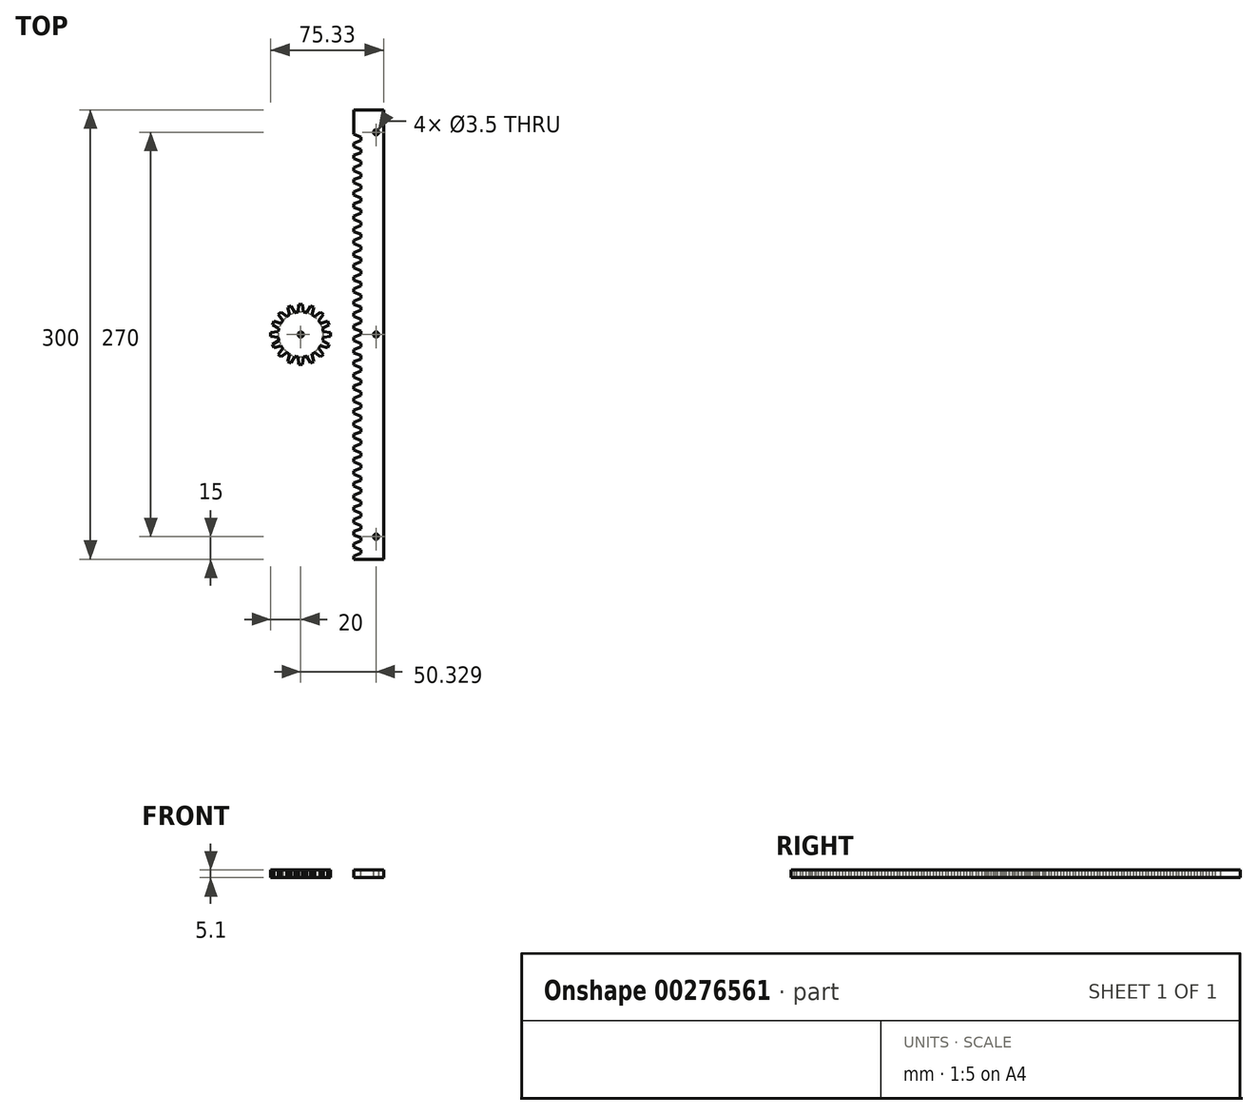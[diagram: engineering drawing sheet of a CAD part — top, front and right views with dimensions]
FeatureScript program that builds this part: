
annotation { "Feature Type Name" : "Feature", "Feature Type Description" : "" }
export const myFeature = defineFeature(function(context is Context, id is Id, definition is map)
    precondition{}
    {
        {
            var Q0;
            Q0=qCreatedBy(makeId("Top.planeOp"),FACE);
            var sketch = newSketch(context, id + "F0", { "sketchPlane" : qUnion([Q0])});
            skCircle(sketch, "E0", {"center": v(0, 0) * mm, "radius": 15 * mm});
            skSolve(sketch);
        }
        {
            var Q0;
            Q0=qSketchRegion(id+"F0",true);
            extrude(context, id + "F1", {"entities" : qUnion([Q0]), "depth" : .1 * mm});
        }
        {
            var Q0;
            Q0=makeQuery(id+"F1.opExtrude","CAP_FACE",FACE,{"disambiguationData":[OSD([sQuery(id+"F0.wireOp",EDGE,"E0")])],"isStart":false});
            var sketch = newSketch(context, id + "F2", { "sketchPlane" : qUnion([Q0])});
            skLineSegment(sketch, "E1", {"start": v(0, 0) * mm, "end": v(4.14, 32.55) * mm, "construction": true});
            skLineSegment(sketch, "E2", {"start": v(0, 0) * mm, "end": v(-4.14, 32.58) * mm, "construction": true});
            skLineSegment(sketch, "E3", {"start": v(-1.9, 14.88) * mm, "end": v(-1.24, 20) * mm});
            skLineSegment(sketch, "E4", {"start": v(-1.24, 20) * mm, "end": v(1.24, 20) * mm});
            skLineSegment(sketch, "E5", {"start": v(1.24, 20) * mm, "end": v(1.9, 14.88) * mm});
            skLineSegment(sketch, "E6.1.0", {"start": v(-7.44, 13.02) * mm, "end": v(-8.8, 18) * mm});
            skLineSegment(sketch, "E6.1.1", {"start": v(-6.5, 18.95) * mm, "end": v(-3.95, 14.47) * mm});
            skLineSegment(sketch, "E6.1.2", {"start": v(-8.8, 18) * mm, "end": v(-6.5, 18.95) * mm});
            skLineSegment(sketch, "E6.2.0", {"start": v(-11.86, 9.18) * mm, "end": v(-15.02, 13.26) * mm});
            skLineSegment(sketch, "E6.2.1", {"start": v(-13.26, 15.02) * mm, "end": v(-9.18, 11.86) * mm});
            skLineSegment(sketch, "E6.2.2", {"start": v(-15.02, 13.26) * mm, "end": v(-13.26, 15.02) * mm});
            skLineSegment(sketch, "E6.3.0", {"start": v(-14.47, 3.95) * mm, "end": v(-18.95, 6.5) * mm});
            skLineSegment(sketch, "E6.3.1", {"start": v(-18, 8.8) * mm, "end": v(-13.02, 7.44) * mm});
            skLineSegment(sketch, "E6.3.2", {"start": v(-18.95, 6.5) * mm, "end": v(-18, 8.8) * mm});
            skLineSegment(sketch, "E6.4.0", {"start": v(-14.88, -1.9) * mm, "end": v(-20, -1.24) * mm});
            skLineSegment(sketch, "E6.4.1", {"start": v(-20, 1.24) * mm, "end": v(-14.88, 1.9) * mm});
            skLineSegment(sketch, "E6.4.2", {"start": v(-20, -1.24) * mm, "end": v(-20, 1.24) * mm});
            skLineSegment(sketch, "E6.5.0", {"start": v(-13.02, -7.44) * mm, "end": v(-18, -8.8) * mm});
            skLineSegment(sketch, "E6.5.1", {"start": v(-18.95, -6.5) * mm, "end": v(-14.47, -3.95) * mm});
            skLineSegment(sketch, "E6.5.2", {"start": v(-18, -8.8) * mm, "end": v(-18.95, -6.5) * mm});
            skLineSegment(sketch, "E6.6.0", {"start": v(-9.18, -11.86) * mm, "end": v(-13.26, -15.02) * mm});
            skLineSegment(sketch, "E6.6.1", {"start": v(-15.02, -13.26) * mm, "end": v(-11.86, -9.18) * mm});
            skLineSegment(sketch, "E6.6.2", {"start": v(-13.26, -15.02) * mm, "end": v(-15.02, -13.26) * mm});
            skLineSegment(sketch, "E6.7.0", {"start": v(-3.95, -14.47) * mm, "end": v(-6.5, -18.95) * mm});
            skLineSegment(sketch, "E6.7.1", {"start": v(-8.8, -18) * mm, "end": v(-7.44, -13.02) * mm});
            skLineSegment(sketch, "E6.7.2", {"start": v(-6.5, -18.95) * mm, "end": v(-8.8, -18) * mm});
            skLineSegment(sketch, "E6.8.0", {"start": v(1.9, -14.88) * mm, "end": v(1.24, -20) * mm});
            skLineSegment(sketch, "E6.8.1", {"start": v(-1.24, -20) * mm, "end": v(-1.9, -14.88) * mm});
            skLineSegment(sketch, "E6.8.2", {"start": v(1.24, -20) * mm, "end": v(-1.24, -20) * mm});
            skLineSegment(sketch, "E6.9.0", {"start": v(7.44, -13.02) * mm, "end": v(8.8, -18) * mm});
            skLineSegment(sketch, "E6.9.1", {"start": v(6.5, -18.95) * mm, "end": v(3.95, -14.47) * mm});
            skLineSegment(sketch, "E6.9.2", {"start": v(8.8, -18) * mm, "end": v(6.5, -18.95) * mm});
            skLineSegment(sketch, "E6.10.0", {"start": v(11.86, -9.18) * mm, "end": v(15.02, -13.26) * mm});
            skLineSegment(sketch, "E6.10.1", {"start": v(13.26, -15.02) * mm, "end": v(9.18, -11.86) * mm});
            skLineSegment(sketch, "E6.10.2", {"start": v(15.02, -13.26) * mm, "end": v(13.26, -15.02) * mm});
            skLineSegment(sketch, "E6.11.0", {"start": v(14.47, -3.95) * mm, "end": v(18.95, -6.5) * mm});
            skLineSegment(sketch, "E6.11.1", {"start": v(18, -8.8) * mm, "end": v(13.02, -7.44) * mm});
            skLineSegment(sketch, "E6.11.2", {"start": v(18.95, -6.5) * mm, "end": v(18, -8.8) * mm});
            skLineSegment(sketch, "E6.12.0", {"start": v(14.88, 1.9) * mm, "end": v(20, 1.24) * mm});
            skLineSegment(sketch, "E6.12.1", {"start": v(20, -1.24) * mm, "end": v(14.88, -1.9) * mm});
            skLineSegment(sketch, "E6.12.2", {"start": v(20, 1.24) * mm, "end": v(20, -1.24) * mm});
            skLineSegment(sketch, "E6.13.0", {"start": v(13.02, 7.44) * mm, "end": v(18, 8.8) * mm});
            skLineSegment(sketch, "E6.13.1", {"start": v(18.95, 6.5) * mm, "end": v(14.47, 3.95) * mm});
            skLineSegment(sketch, "E6.13.2", {"start": v(18, 8.8) * mm, "end": v(18.95, 6.5) * mm});
            skLineSegment(sketch, "E6.14.0", {"start": v(9.18, 11.86) * mm, "end": v(13.26, 15.02) * mm});
            skLineSegment(sketch, "E6.14.1", {"start": v(15.02, 13.26) * mm, "end": v(11.86, 9.18) * mm});
            skLineSegment(sketch, "E6.14.2", {"start": v(13.26, 15.02) * mm, "end": v(15.02, 13.26) * mm});
            skLineSegment(sketch, "E6.15.0", {"start": v(3.95, 14.47) * mm, "end": v(6.5, 18.95) * mm});
            skLineSegment(sketch, "E6.15.1", {"start": v(8.8, 18) * mm, "end": v(7.44, 13.02) * mm});
            skLineSegment(sketch, "E6.15.2", {"start": v(6.5, 18.95) * mm, "end": v(8.8, 18) * mm});
            skPoint(sketch, "E6.center", {"position": v(0, 0) * mm});
            skCircle(sketch, "E7", {"center": v(0, 0) * mm, "radius": 15.15 * mm});
            skSolve(sketch);
        }
        {
            var Q0;
            Q0=qSketchRegion(id+"F2",true);
            extrude(context, id + "F3", {"entities" : qUnion([Q0]), "operationType" : NewBodyOperationType.ADD, "depth" : 5 * mm});
        }
        {
            var Q0;
            Q0=qCreatedBy(makeId("Top.planeOp"),FACE);
            var sketch = newSketch(context, id + "F4", { "sketchPlane" : qUnion([Q0])});
            skLineSegment(sketch, "E8.bottom", {"start": v(35.33, -150) * mm, "end": v(55.33, -150) * mm});
            skLineSegment(sketch, "E8.top", {"start": v(35.33, 150) * mm, "end": v(55.33, 150) * mm});
            skLineSegment(sketch, "E8.left", {"start": v(35.33, -150) * mm, "end": v(35.33, 150) * mm});
            skLineSegment(sketch, "E8.right", {"start": v(55.33, -150) * mm, "end": v(55.33, 150) * mm});
            skPoint(sketch, "E8.middle", {"position": v(45.33, 0) * mm});
            skSolve(sketch);
        }
        {
            var Q0;
            Q0=qSketchRegion(id+"F4",true);
            extrude(context, id + "F5", {"entities" : qUnion([Q0]), "depth" : 5 * mm});
        }
        {
            var Q0;
            Q0=makeQuery(id+"F5.opExtrude","CAP_FACE",FACE,{"disambiguationData":[OSD([sQuery(id+"F4.wireOp",EDGE,"E8.bottom"),sQuery(id+"F4.wireOp",EDGE,"E8.top"),sQuery(id+"F4.wireOp",EDGE,"E8.left"),sQuery(id+"F4.wireOp",EDGE,"E8.right")])],"isStart":false});
            var sketch = newSketch(context, id + "F6", { "sketchPlane" : qUnion([Q0])});
            skLineSegment(sketch, "E9", {"start": v(35.33, -147.77) * mm, "end": v(40.33, -145.95) * mm});
            skLineSegment(sketch, "E10", {"start": v(40.33, -145.95) * mm, "end": v(40.33, -143.72) * mm});
            skLineSegment(sketch, "E11", {"start": v(40.33, -143.72) * mm, "end": v(35.33, -141.9) * mm});
            skLineSegment(sketch, "E12", {"start": v(35.33, -147.77) * mm, "end": v(35.33, -150) * mm});
            skLineSegment(sketch, "E13.1.0.0", {"start": v(40.33, -135.62) * mm, "end": v(35.33, -133.8) * mm});
            skLineSegment(sketch, "E13.1.0.1", {"start": v(35.33, -139.67) * mm, "end": v(40.33, -137.85) * mm});
            skLineSegment(sketch, "E13.1.0.2", {"start": v(35.33, -139.67) * mm, "end": v(35.33, -141.9) * mm});
            skLineSegment(sketch, "E13.1.0.3", {"start": v(40.33, -137.85) * mm, "end": v(40.33, -135.62) * mm});
            skLineSegment(sketch, "E13.2.0.0", {"start": v(40.33, -127.51) * mm, "end": v(35.33, -125.7) * mm});
            skLineSegment(sketch, "E13.2.0.1", {"start": v(35.33, -131.56) * mm, "end": v(40.33, -129.75) * mm});
            skLineSegment(sketch, "E13.2.0.2", {"start": v(35.33, -131.56) * mm, "end": v(35.33, -133.8) * mm});
            skLineSegment(sketch, "E13.2.0.3", {"start": v(40.33, -129.75) * mm, "end": v(40.33, -127.51) * mm});
            skLineSegment(sketch, "E13.3.0.0", {"start": v(40.33, -119.41) * mm, "end": v(35.33, -117.6) * mm});
            skLineSegment(sketch, "E13.3.0.1", {"start": v(35.33, -123.46) * mm, "end": v(40.33, -121.64) * mm});
            skLineSegment(sketch, "E13.3.0.2", {"start": v(35.33, -123.46) * mm, "end": v(35.33, -125.7) * mm});
            skLineSegment(sketch, "E13.3.0.3", {"start": v(40.33, -121.64) * mm, "end": v(40.33, -119.41) * mm});
            skLineSegment(sketch, "E13.4.0.0", {"start": v(40.33, -111.31) * mm, "end": v(35.33, -109.5) * mm});
            skLineSegment(sketch, "E13.4.0.1", {"start": v(35.33, -115.36) * mm, "end": v(40.33, -113.54) * mm});
            skLineSegment(sketch, "E13.4.0.2", {"start": v(35.33, -115.36) * mm, "end": v(35.33, -117.6) * mm});
            skLineSegment(sketch, "E13.4.0.3", {"start": v(40.33, -113.54) * mm, "end": v(40.33, -111.31) * mm});
            skLineSegment(sketch, "E13.5.0.0", {"start": v(40.33, -103.2) * mm, "end": v(35.33, -101.39) * mm});
            skLineSegment(sketch, "E13.5.0.1", {"start": v(35.33, -107.26) * mm, "end": v(40.33, -105.44) * mm});
            skLineSegment(sketch, "E13.5.0.2", {"start": v(35.33, -107.26) * mm, "end": v(35.33, -109.5) * mm});
            skLineSegment(sketch, "E13.5.0.3", {"start": v(40.33, -105.44) * mm, "end": v(40.33, -103.2) * mm});
            skLineSegment(sketch, "E13.6.0.0", {"start": v(40.33, -95.1) * mm, "end": v(35.33, -93.29) * mm});
            skLineSegment(sketch, "E13.6.0.1", {"start": v(35.33, -99.16) * mm, "end": v(40.33, -97.34) * mm});
            skLineSegment(sketch, "E13.6.0.2", {"start": v(35.33, -99.16) * mm, "end": v(35.33, -101.39) * mm});
            skLineSegment(sketch, "E13.6.0.3", {"start": v(40.33, -97.34) * mm, "end": v(40.33, -95.1) * mm});
            skLineSegment(sketch, "E13.7.0.0", {"start": v(40.33, -87) * mm, "end": v(35.33, -85.18) * mm});
            skLineSegment(sketch, "E13.7.0.1", {"start": v(35.33, -91.05) * mm, "end": v(40.33, -89.24) * mm});
            skLineSegment(sketch, "E13.7.0.2", {"start": v(35.33, -91.05) * mm, "end": v(35.33, -93.29) * mm});
            skLineSegment(sketch, "E13.7.0.3", {"start": v(40.33, -89.24) * mm, "end": v(40.33, -87) * mm});
            skLineSegment(sketch, "E13.8.0.0", {"start": v(40.33, -78.9) * mm, "end": v(35.33, -77.08) * mm});
            skLineSegment(sketch, "E13.8.0.1", {"start": v(35.33, -82.95) * mm, "end": v(40.33, -81.13) * mm});
            skLineSegment(sketch, "E13.8.0.2", {"start": v(35.33, -82.95) * mm, "end": v(35.33, -85.18) * mm});
            skLineSegment(sketch, "E13.8.0.3", {"start": v(40.33, -81.13) * mm, "end": v(40.33, -78.9) * mm});
            skLineSegment(sketch, "E13.9.0.0", {"start": v(40.33, -70.8) * mm, "end": v(35.33, -68.98) * mm});
            skLineSegment(sketch, "E13.9.0.1", {"start": v(35.33, -74.85) * mm, "end": v(40.33, -73.03) * mm});
            skLineSegment(sketch, "E13.9.0.2", {"start": v(35.33, -74.85) * mm, "end": v(35.33, -77.08) * mm});
            skLineSegment(sketch, "E13.9.0.3", {"start": v(40.33, -73.03) * mm, "end": v(40.33, -70.8) * mm});
            skLineSegment(sketch, "E13.10.0.0", {"start": v(40.33, -62.7) * mm, "end": v(35.33, -60.88) * mm});
            skLineSegment(sketch, "E13.10.0.1", {"start": v(35.33, -66.75) * mm, "end": v(40.33, -64.93) * mm});
            skLineSegment(sketch, "E13.10.0.2", {"start": v(35.33, -66.75) * mm, "end": v(35.33, -68.98) * mm});
            skLineSegment(sketch, "E13.10.0.3", {"start": v(40.33, -64.93) * mm, "end": v(40.33, -62.7) * mm});
            skLineSegment(sketch, "E13.11.0.0", {"start": v(40.33, -54.6) * mm, "end": v(35.33, -52.78) * mm});
            skLineSegment(sketch, "E13.11.0.1", {"start": v(35.33, -58.65) * mm, "end": v(40.33, -56.83) * mm});
            skLineSegment(sketch, "E13.11.0.2", {"start": v(35.33, -58.65) * mm, "end": v(35.33, -60.88) * mm});
            skLineSegment(sketch, "E13.11.0.3", {"start": v(40.33, -56.83) * mm, "end": v(40.33, -54.6) * mm});
            skLineSegment(sketch, "E13.12.0.0", {"start": v(40.33, -46.5) * mm, "end": v(35.33, -44.67) * mm});
            skLineSegment(sketch, "E13.12.0.1", {"start": v(35.33, -50.54) * mm, "end": v(40.33, -48.73) * mm});
            skLineSegment(sketch, "E13.12.0.2", {"start": v(35.33, -50.54) * mm, "end": v(35.33, -52.78) * mm});
            skLineSegment(sketch, "E13.12.0.3", {"start": v(40.33, -48.73) * mm, "end": v(40.33, -46.5) * mm});
            skLineSegment(sketch, "E13.13.0.0", {"start": v(40.33, -38.4) * mm, "end": v(35.33, -36.57) * mm});
            skLineSegment(sketch, "E13.13.0.1", {"start": v(35.33, -42.44) * mm, "end": v(40.33, -40.62) * mm});
            skLineSegment(sketch, "E13.13.0.2", {"start": v(35.33, -42.44) * mm, "end": v(35.33, -44.67) * mm});
            skLineSegment(sketch, "E13.13.0.3", {"start": v(40.33, -40.62) * mm, "end": v(40.33, -38.4) * mm});
            skLineSegment(sketch, "E13.14.0.0", {"start": v(40.33, -30.3) * mm, "end": v(35.33, -28.47) * mm});
            skLineSegment(sketch, "E13.14.0.1", {"start": v(35.33, -34.34) * mm, "end": v(40.33, -32.52) * mm});
            skLineSegment(sketch, "E13.14.0.2", {"start": v(35.33, -34.34) * mm, "end": v(35.33, -36.57) * mm});
            skLineSegment(sketch, "E13.14.0.3", {"start": v(40.33, -32.52) * mm, "end": v(40.33, -30.3) * mm});
            skLineSegment(sketch, "E13.15.0.0", {"start": v(40.33, -22.19) * mm, "end": v(35.33, -20.37) * mm});
            skLineSegment(sketch, "E13.15.0.1", {"start": v(35.33, -26.24) * mm, "end": v(40.33, -24.42) * mm});
            skLineSegment(sketch, "E13.15.0.2", {"start": v(35.33, -26.24) * mm, "end": v(35.33, -28.47) * mm});
            skLineSegment(sketch, "E13.15.0.3", {"start": v(40.33, -24.42) * mm, "end": v(40.33, -22.19) * mm});
            skLineSegment(sketch, "E13.16.0.0", {"start": v(40.33, -14.09) * mm, "end": v(35.33, -12.27) * mm});
            skLineSegment(sketch, "E13.16.0.1", {"start": v(35.33, -18.14) * mm, "end": v(40.33, -16.32) * mm});
            skLineSegment(sketch, "E13.16.0.2", {"start": v(35.33, -18.14) * mm, "end": v(35.33, -20.37) * mm});
            skLineSegment(sketch, "E13.16.0.3", {"start": v(40.33, -16.32) * mm, "end": v(40.33, -14.09) * mm});
            skLineSegment(sketch, "E13.17.0.0", {"start": v(40.33, -5.98) * mm, "end": v(35.33, -4.16) * mm});
            skLineSegment(sketch, "E13.17.0.1", {"start": v(35.33, -10.03) * mm, "end": v(40.33, -8.22) * mm});
            skLineSegment(sketch, "E13.17.0.2", {"start": v(35.33, -10.03) * mm, "end": v(35.33, -12.27) * mm});
            skLineSegment(sketch, "E13.17.0.3", {"start": v(40.33, -8.22) * mm, "end": v(40.33, -5.98) * mm});
            skLineSegment(sketch, "E13.18.0.0", {"start": v(40.33, 2.12) * mm, "end": v(35.33, 3.94) * mm});
            skLineSegment(sketch, "E13.18.0.1", {"start": v(35.33, -1.93) * mm, "end": v(40.33, -0.11) * mm});
            skLineSegment(sketch, "E13.18.0.2", {"start": v(35.33, -1.93) * mm, "end": v(35.33, -4.16) * mm});
            skLineSegment(sketch, "E13.18.0.3", {"start": v(40.33, -0.11) * mm, "end": v(40.33, 2.12) * mm});
            skLineSegment(sketch, "E13.19.0.0", {"start": v(40.33, 10.22) * mm, "end": v(35.33, 12.04) * mm});
            skLineSegment(sketch, "E13.19.0.1", {"start": v(35.33, 6.17) * mm, "end": v(40.33, 7.99) * mm});
            skLineSegment(sketch, "E13.19.0.2", {"start": v(35.33, 6.17) * mm, "end": v(35.33, 3.94) * mm});
            skLineSegment(sketch, "E13.19.0.3", {"start": v(40.33, 7.99) * mm, "end": v(40.33, 10.22) * mm});
            skLineSegment(sketch, "E13.20.0.0", {"start": v(40.33, 18.32) * mm, "end": v(35.33, 20.14) * mm});
            skLineSegment(sketch, "E13.20.0.1", {"start": v(35.33, 14.27) * mm, "end": v(40.33, 16.1) * mm});
            skLineSegment(sketch, "E13.20.0.2", {"start": v(35.33, 14.27) * mm, "end": v(35.33, 12.04) * mm});
            skLineSegment(sketch, "E13.20.0.3", {"start": v(40.33, 16.1) * mm, "end": v(40.33, 18.32) * mm});
            skLineSegment(sketch, "E13.21.0.0", {"start": v(40.33, 26.42) * mm, "end": v(35.33, 28.24) * mm});
            skLineSegment(sketch, "E13.21.0.1", {"start": v(35.33, 22.37) * mm, "end": v(40.33, 24.2) * mm});
            skLineSegment(sketch, "E13.21.0.2", {"start": v(35.33, 22.37) * mm, "end": v(35.33, 20.14) * mm});
            skLineSegment(sketch, "E13.21.0.3", {"start": v(40.33, 24.2) * mm, "end": v(40.33, 26.42) * mm});
            skLineSegment(sketch, "E13.22.0.0", {"start": v(40.33, 34.53) * mm, "end": v(35.33, 36.35) * mm});
            skLineSegment(sketch, "E13.22.0.1", {"start": v(35.33, 30.48) * mm, "end": v(40.33, 32.3) * mm});
            skLineSegment(sketch, "E13.22.0.2", {"start": v(35.33, 30.48) * mm, "end": v(35.33, 28.24) * mm});
            skLineSegment(sketch, "E13.22.0.3", {"start": v(40.33, 32.3) * mm, "end": v(40.33, 34.53) * mm});
            skLineSegment(sketch, "E13.23.0.0", {"start": v(40.33, 42.63) * mm, "end": v(35.33, 44.45) * mm});
            skLineSegment(sketch, "E13.23.0.1", {"start": v(35.33, 38.58) * mm, "end": v(40.33, 40.4) * mm});
            skLineSegment(sketch, "E13.23.0.2", {"start": v(35.33, 38.58) * mm, "end": v(35.33, 36.35) * mm});
            skLineSegment(sketch, "E13.23.0.3", {"start": v(40.33, 40.4) * mm, "end": v(40.33, 42.63) * mm});
            skLineSegment(sketch, "E13.24.0.0", {"start": v(40.33, 50.73) * mm, "end": v(35.33, 52.55) * mm});
            skLineSegment(sketch, "E13.24.0.1", {"start": v(35.33, 46.68) * mm, "end": v(40.33, 48.5) * mm});
            skLineSegment(sketch, "E13.24.0.2", {"start": v(35.33, 46.68) * mm, "end": v(35.33, 44.45) * mm});
            skLineSegment(sketch, "E13.24.0.3", {"start": v(40.33, 48.5) * mm, "end": v(40.33, 50.73) * mm});
            skLineSegment(sketch, "E13.25.0.0", {"start": v(40.33, 58.83) * mm, "end": v(35.33, 60.65) * mm});
            skLineSegment(sketch, "E13.25.0.1", {"start": v(35.33, 54.78) * mm, "end": v(40.33, 56.6) * mm});
            skLineSegment(sketch, "E13.25.0.2", {"start": v(35.33, 54.78) * mm, "end": v(35.33, 52.55) * mm});
            skLineSegment(sketch, "E13.25.0.3", {"start": v(40.33, 56.6) * mm, "end": v(40.33, 58.83) * mm});
            skLineSegment(sketch, "E13.26.0.0", {"start": v(40.33, 66.93) * mm, "end": v(35.33, 68.75) * mm});
            skLineSegment(sketch, "E13.26.0.1", {"start": v(35.33, 62.88) * mm, "end": v(40.33, 64.7) * mm});
            skLineSegment(sketch, "E13.26.0.2", {"start": v(35.33, 62.88) * mm, "end": v(35.33, 60.65) * mm});
            skLineSegment(sketch, "E13.26.0.3", {"start": v(40.33, 64.7) * mm, "end": v(40.33, 66.93) * mm});
            skLineSegment(sketch, "E13.27.0.0", {"start": v(40.33, 75.04) * mm, "end": v(35.33, 76.86) * mm});
            skLineSegment(sketch, "E13.27.0.1", {"start": v(35.33, 70.99) * mm, "end": v(40.33, 72.8) * mm});
            skLineSegment(sketch, "E13.27.0.2", {"start": v(35.33, 70.99) * mm, "end": v(35.33, 68.75) * mm});
            skLineSegment(sketch, "E13.27.0.3", {"start": v(40.33, 72.8) * mm, "end": v(40.33, 75.04) * mm});
            skLineSegment(sketch, "E13.28.0.0", {"start": v(40.33, 83.14) * mm, "end": v(35.33, 84.96) * mm});
            skLineSegment(sketch, "E13.28.0.1", {"start": v(35.33, 79.09) * mm, "end": v(40.33, 80.9) * mm});
            skLineSegment(sketch, "E13.28.0.2", {"start": v(35.33, 79.09) * mm, "end": v(35.33, 76.86) * mm});
            skLineSegment(sketch, "E13.28.0.3", {"start": v(40.33, 80.9) * mm, "end": v(40.33, 83.14) * mm});
            skLineSegment(sketch, "E13.29.0.0", {"start": v(40.33, 91.24) * mm, "end": v(35.33, 93.06) * mm});
            skLineSegment(sketch, "E13.29.0.1", {"start": v(35.33, 87.19) * mm, "end": v(40.33, 89) * mm});
            skLineSegment(sketch, "E13.29.0.2", {"start": v(35.33, 87.19) * mm, "end": v(35.33, 84.96) * mm});
            skLineSegment(sketch, "E13.29.0.3", {"start": v(40.33, 89) * mm, "end": v(40.33, 91.24) * mm});
            skLineSegment(sketch, "E13.direction1", {"start": v(35.33, -141.9) * mm, "end": v(35.33, -133.8) * mm, "construction": true});
            skLineSegment(sketch, "E14.0.30.0", {"start": v(40.33, 99.34) * mm, "end": v(35.33, 101.16) * mm});
            skLineSegment(sketch, "E14.3.30.0", {"start": v(35.33, 95.3) * mm, "end": v(40.33, 97.11) * mm});
            skLineSegment(sketch, "E14.6.30.0", {"start": v(35.33, 95.3) * mm, "end": v(35.33, 93.06) * mm});
            skLineSegment(sketch, "E14.9.30.0", {"start": v(40.33, 97.11) * mm, "end": v(40.33, 99.34) * mm});
            skLineSegment(sketch, "E14.0.31.0", {"start": v(40.33, 107.44) * mm, "end": v(35.33, 109.26) * mm});
            skLineSegment(sketch, "E14.3.31.0", {"start": v(35.33, 103.4) * mm, "end": v(40.33, 105.21) * mm});
            skLineSegment(sketch, "E14.6.31.0", {"start": v(35.33, 103.4) * mm, "end": v(35.33, 101.16) * mm});
            skLineSegment(sketch, "E14.9.31.0", {"start": v(40.33, 105.21) * mm, "end": v(40.33, 107.44) * mm});
            skLineSegment(sketch, "E14.0.32.0", {"start": v(40.33, 115.55) * mm, "end": v(35.33, 117.37) * mm});
            skLineSegment(sketch, "E14.3.32.0", {"start": v(35.33, 111.5) * mm, "end": v(40.33, 113.31) * mm});
            skLineSegment(sketch, "E14.6.32.0", {"start": v(35.33, 111.5) * mm, "end": v(35.33, 109.26) * mm});
            skLineSegment(sketch, "E14.9.32.0", {"start": v(40.33, 113.31) * mm, "end": v(40.33, 115.55) * mm});
            skLineSegment(sketch, "E14.0.33.0", {"start": v(40.33, 123.65) * mm, "end": v(35.33, 125.47) * mm});
            skLineSegment(sketch, "E14.3.33.0", {"start": v(35.33, 119.6) * mm, "end": v(40.33, 121.42) * mm});
            skLineSegment(sketch, "E14.6.33.0", {"start": v(35.33, 119.6) * mm, "end": v(35.33, 117.37) * mm});
            skLineSegment(sketch, "E14.9.33.0", {"start": v(40.33, 121.42) * mm, "end": v(40.33, 123.65) * mm});
            skLineSegment(sketch, "E14.0.34.0", {"start": v(40.33, 131.75) * mm, "end": v(35.33, 133.57) * mm});
            skLineSegment(sketch, "E14.3.34.0", {"start": v(35.33, 127.7) * mm, "end": v(40.33, 129.52) * mm});
            skLineSegment(sketch, "E14.6.34.0", {"start": v(35.33, 127.7) * mm, "end": v(35.33, 125.47) * mm});
            skLineSegment(sketch, "E14.9.34.0", {"start": v(40.33, 129.52) * mm, "end": v(40.33, 131.75) * mm});
            skLineSegment(sketch, "E15", {"start": v(35.33, -150) * mm, "end": v(35.33, 133.57) * mm});
            skSolve(sketch);
        }
        {
            var Q0;
            Q0=qSketchRegion(id+"F6",true);
            extrude(context, id + "F7", {"entities" : qUnion([Q0]), "operationType" : NewBodyOperationType.REMOVE, "oppositeDirection" : true, "depth" : 5 * mm});
        }
        {
            var Q0;
            Q0=makeQuery(id+"F5.opExtrude","CAP_FACE",FACE,{"disambiguationData":[OSD([sQuery(id+"F4.wireOp",EDGE,"E8.bottom"),sQuery(id+"F4.wireOp",EDGE,"E8.top"),sQuery(id+"F4.wireOp",EDGE,"E8.left"),sQuery(id+"F4.wireOp",EDGE,"E8.right")])],"isStart":false});
            var sketch = newSketch(context, id + "F8", { "sketchPlane" : qUnion([Q0])});
            skPoint(sketch, "E16", {"position": v(50.33, -135) * mm});
            skPoint(sketch, "E17", {"position": v(50.33, 0) * mm});
            skPoint(sketch, "E18", {"position": v(50.33, 135) * mm});
            skSolve(sketch);
        }
        {
            var Q0;
            Q0=makeQuery(id+"F3.opExtrude","CAP_FACE",FACE,{"disambiguationData":[OSD([sQuery(id+"F2.wireOp",EDGE,"E3"),sQuery(id+"F2.wireOp",EDGE,"E4"),sQuery(id+"F2.wireOp",EDGE,"E5"),sQuery(id+"F2.wireOp",EDGE,"E6.1.0"),sQuery(id+"F2.wireOp",EDGE,"E6.1.1"),sQuery(id+"F2.wireOp",EDGE,"E6.1.2"),sQuery(id+"F2.wireOp",EDGE,"E6.2.0"),sQuery(id+"F2.wireOp",EDGE,"E6.2.1"),sQuery(id+"F2.wireOp",EDGE,"E6.2.2"),sQuery(id+"F2.wireOp",EDGE,"E6.3.0"),sQuery(id+"F2.wireOp",EDGE,"E6.3.1"),sQuery(id+"F2.wireOp",EDGE,"E6.3.2"),sQuery(id+"F2.wireOp",EDGE,"E6.4.0"),sQuery(id+"F2.wireOp",EDGE,"E6.4.1"),sQuery(id+"F2.wireOp",EDGE,"E6.4.2"),sQuery(id+"F2.wireOp",EDGE,"E6.5.0"),sQuery(id+"F2.wireOp",EDGE,"E6.5.1"),sQuery(id+"F2.wireOp",EDGE,"E6.5.2"),sQuery(id+"F2.wireOp",EDGE,"E6.6.0"),sQuery(id+"F2.wireOp",EDGE,"E6.6.1"),sQuery(id+"F2.wireOp",EDGE,"E6.6.2"),sQuery(id+"F2.wireOp",EDGE,"E6.7.0"),sQuery(id+"F2.wireOp",EDGE,"E6.7.1"),sQuery(id+"F2.wireOp",EDGE,"E6.7.2"),sQuery(id+"F2.wireOp",EDGE,"E6.8.0"),sQuery(id+"F2.wireOp",EDGE,"E6.8.1"),sQuery(id+"F2.wireOp",EDGE,"E6.8.2"),sQuery(id+"F2.wireOp",EDGE,"E6.9.0"),sQuery(id+"F2.wireOp",EDGE,"E6.9.1"),sQuery(id+"F2.wireOp",EDGE,"E6.9.2"),sQuery(id+"F2.wireOp",EDGE,"E6.10.0"),sQuery(id+"F2.wireOp",EDGE,"E6.10.1"),sQuery(id+"F2.wireOp",EDGE,"E6.10.2"),sQuery(id+"F2.wireOp",EDGE,"E6.11.0"),sQuery(id+"F2.wireOp",EDGE,"E6.11.1"),sQuery(id+"F2.wireOp",EDGE,"E6.11.2"),sQuery(id+"F2.wireOp",EDGE,"E6.12.0"),sQuery(id+"F2.wireOp",EDGE,"E6.12.1"),sQuery(id+"F2.wireOp",EDGE,"E6.12.2"),sQuery(id+"F2.wireOp",EDGE,"E6.13.0"),sQuery(id+"F2.wireOp",EDGE,"E6.13.1"),sQuery(id+"F2.wireOp",EDGE,"E6.13.2"),sQuery(id+"F2.wireOp",EDGE,"E6.14.0"),sQuery(id+"F2.wireOp",EDGE,"E6.14.1"),sQuery(id+"F2.wireOp",EDGE,"E6.14.2"),sQuery(id+"F2.wireOp",EDGE,"E6.15.0"),sQuery(id+"F2.wireOp",EDGE,"E6.15.1"),sQuery(id+"F2.wireOp",EDGE,"E6.15.2"),sQuery(id+"F2.wireOp",EDGE,"E6.16.0"),sQuery(id+"F2.wireOp",EDGE,"E6.16.1"),sQuery(id+"F2.wireOp",EDGE,"E6.16.2"),sQuery(id+"F2.wireOp",EDGE,"E6.17.0"),sQuery(id+"F2.wireOp",EDGE,"E6.17.1"),sQuery(id+"F2.wireOp",EDGE,"E6.17.2"),sQuery(id+"F2.wireOp",EDGE,"E6.18.0"),sQuery(id+"F2.wireOp",EDGE,"E6.18.1"),sQuery(id+"F2.wireOp",EDGE,"E6.18.2"),sQuery(id+"F2.wireOp",EDGE,"E6.19.0"),sQuery(id+"F2.wireOp",EDGE,"E6.19.1"),sQuery(id+"F2.wireOp",EDGE,"E6.19.2"),sQuery(id+"F2.wireOp",EDGE,"9fe82336-65db-4577-8fdd-86a6f8489eb6.1.20.0"),sQuery(id+"F2.wireOp",EDGE,"9fe82336-65db-4577-8fdd-86a6f8489eb6.3.20.0"),sQuery(id+"F2.wireOp",EDGE,"9fe82336-65db-4577-8fdd-86a6f8489eb6.6.20.0"),sQuery(id+"F2.wireOp",EDGE,"E7"),sQuery(id+"F2.wireOp",EDGE,"8499c75c-cf97-4fb5-be00-e9500dcdae99.1.21.0"),sQuery(id+"F2.wireOp",EDGE,"8499c75c-cf97-4fb5-be00-e9500dcdae99.3.21.0"),sQuery(id+"F2.wireOp",EDGE,"8499c75c-cf97-4fb5-be00-e9500dcdae99.6.21.0")])],"isStart":false});
            var sketch = newSketch(context, id + "F9", { "sketchPlane" : qUnion([Q0])});
            skPoint(sketch, "E19", {"position": v(0, 0) * mm});
            skSolve(sketch);
        }
        {
            var Q0;
            Q0=sQuery(id+"F9.wireOp",VERTEX,"E19");
            var Q1;
            Q1=makeQuery(id+"F1.opExtrude","SWEPT_BODY",BODY,{"disambiguationData":[OSD([sQuery(id+"F0.wireOp",EDGE,"E0")])]});
            var Q2;
            Q2=makeQuery(id+"F5.opExtrude","SWEPT_BODY",BODY,{"disambiguationData":[OSD([sQuery(id+"F4.wireOp",EDGE,"E8.bottom"),sQuery(id+"F4.wireOp",EDGE,"E8.top"),sQuery(id+"F4.wireOp",EDGE,"E8.left"),sQuery(id+"F4.wireOp",EDGE,"E8.right")])]});
            hole(context, id + "F10", {"style" : HoleStyle.SIMPLE, "endStyle" : HoleEndStyle.THROUGH, "holeDiameter" : 3.5 * mm, "tappedDepth" : 12 * mm, "tapClearance" : 3, "locations" : qUnion([Q0]), "scope" : qUnion([Q1, Q2])});
        }
        {
            var Q0;
            Q0=sQuery(id+"F8.wireOp",VERTEX,"E18");
            var Q1;
            Q1=sQuery(id+"F8.wireOp",VERTEX,"E17");
            var Q2;
            Q2=sQuery(id+"F8.wireOp",VERTEX,"E16");
            var Q3;
            Q3=makeQuery(id+"F5.opExtrude","SWEPT_BODY",BODY,{"disambiguationData":[OSD([sQuery(id+"F4.wireOp",EDGE,"E8.bottom"),sQuery(id+"F4.wireOp",EDGE,"E8.top"),sQuery(id+"F4.wireOp",EDGE,"E8.left"),sQuery(id+"F4.wireOp",EDGE,"E8.right")])]});
            hole(context, id + "F11", {"style" : HoleStyle.SIMPLE, "endStyle" : HoleEndStyle.THROUGH, "holeDiameter" : 3.5 * mm, "isTappedThrough" : true, "tappedDepth" : 12 * mm, "tapClearance" : 3, "locations" : qUnion([Q0, Q1, Q2]), "scope" : qUnion([Q3])});
        }
    });
